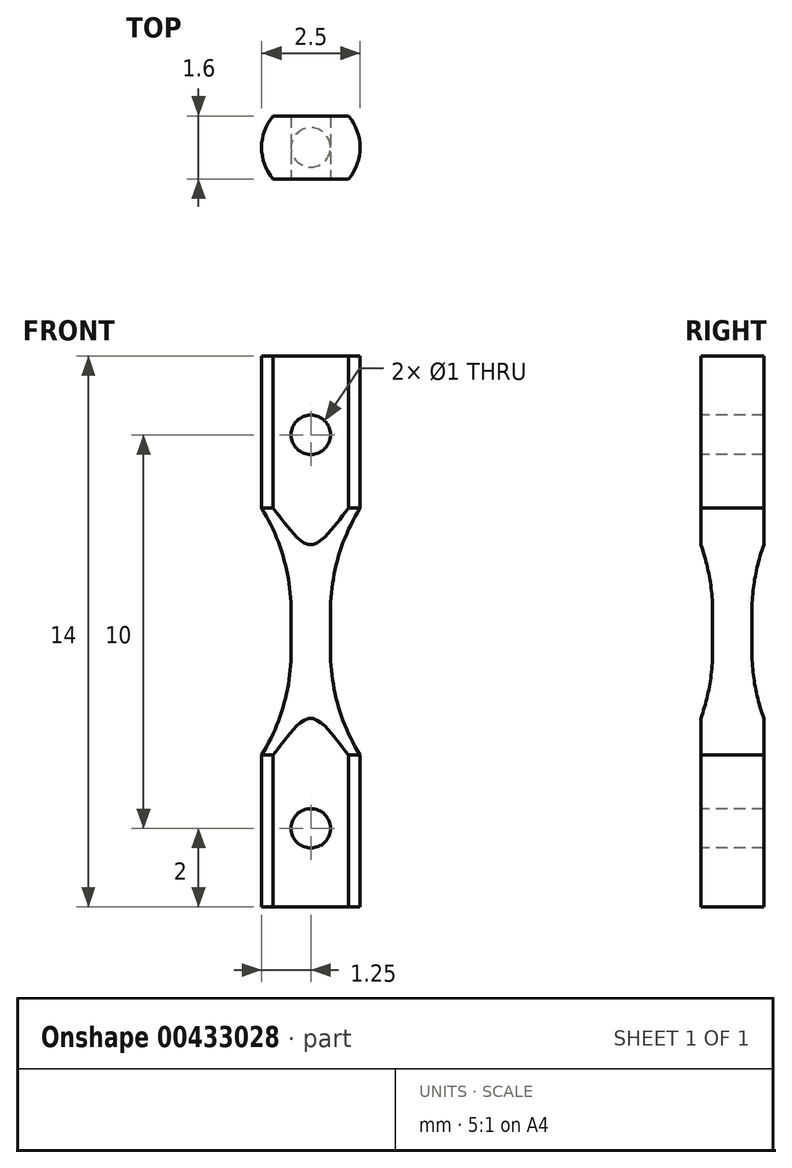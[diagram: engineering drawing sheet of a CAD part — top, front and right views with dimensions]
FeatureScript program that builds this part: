
annotation { "Feature Type Name" : "Feature", "Feature Type Description" : "" }
export const myFeature = defineFeature(function(context is Context, id is Id, definition is map)
    precondition{}
    {
        {
            var Q0;
            Q0=qCreatedBy(makeId("Front.planeOp"),FACE);
            var sketch = newSketch(context, id + "F0", { "sketchPlane" : qUnion([Q0])});
            skLineSegment(sketch, "E0", {"start": v(0, 7) * mm, "end": v(0, 0) * mm});
            skPoint(sketch, "E1", {"position": v(5.5, 0.5) * mm});
            skArc(sketch, "E2", {"start": v(0.5, 0.5) * mm, "mid": v(1.96, 4.04) * mm, "end": v(5.5, 5.5) * mm, "construction": true});
            skLineSegment(sketch, "E3", {"start": v(0, 7) * mm, "end": v(1.25, 7) * mm});
            skLineSegment(sketch, "E4", {"start": v(1.25, 7) * mm, "end": v(1.25, 3.13) * mm});
            skArc(sketch, "E5", {"start": v(0.5, 0.5) * mm, "mid": v(0.7, 1.87) * mm, "end": v(1.25, 3.13) * mm});
            skLineSegment(sketch, "E6.MirrorCS", {"start": v(0, -7) * mm, "end": v(0, 0) * mm});
            skArc(sketch, "E7.MirrorCS", {"start": v(0.5, -0.5) * mm, "mid": v(1.96, -4.04) * mm, "end": v(5.5, -5.5) * mm, "construction": true});
            skLineSegment(sketch, "E8.MirrorCS", {"start": v(1.25, -7) * mm, "end": v(1.25, -3.13) * mm});
            skLineSegment(sketch, "E9.MirrorCS", {"start": v(0, -7) * mm, "end": v(1.25, -7) * mm});
            skArc(sketch, "E10", {"start": v(0.5, -0.5) * mm, "mid": v(0.7, -1.87) * mm, "end": v(1.25, -3.13) * mm});
            skLineSegment(sketch, "E11", {"start": v(0.5, 0.5) * mm, "end": v(0.5, 0.5) * mm});
            skLineSegment(sketch, "E12", {"start": v(0.5, -0.5) * mm, "end": v(0.5, -0.5) * mm});
            skLineSegment(sketch, "E13", {"start": v(0.5, 0.5) * mm, "end": v(0.5, -0.5) * mm});
            skSolve(sketch);
        }
        {
            var Q0;
            {var subQ2=sQuery(id+"F0.wireOp",EDGE,"EKo1FYz1-TvUf-vg46-3QCV-TdD0xKtM2FVf");Q0=makeQuery(id+"F0.imprint","IMPRINT",FACE,{"disambiguationData":[TD([[makeQuery(id+"F0.imprint","IMPRINT",EDGE,{"derivedFrom":subQ2}),1.0]])]});}
            var Q1;
            {var subQ0=sQuery(id+"F0.wireOp",EDGE,"EKo1FYz1-TvUf-vg46-3QCV-TdD0xKtM2FVf");Q1=makeQuery(id+"F0.imprint","IMPRINT",FACE,{"disambiguationData":[TD([[makeQuery(id+"F0.imprint","IMPRINT",EDGE,{"derivedFrom":subQ0}),-1.0]])]});}
            var Q2;
            {var subQ1=sQuery(id+"F0.wireOp",EDGE,"E3");Q2=makeQuery(id+"F0.imprint","IMPRINT",FACE,{"disambiguationData":[TD([[makeQuery(id+"F0.imprint","IMPRINT",EDGE,{"derivedFrom":subQ1}),-1.0]])]});}
            var Q3;
            Q3=sQuery(id+"F0.wireOp",EDGE,"E0");
            revolve(context, id + "F1", {"entities" : qUnion([Q0, Q1, Q2]), "axis" : qUnion([Q3]), "revolveType" : RevolveType.FULL});
        }
        {
            var Q0;
            Q0=qCreatedBy(makeId("Front.planeOp"),FACE);
            var sketch = newSketch(context, id + "F2", { "sketchPlane" : qUnion([Q0])});
            skLineSegment(sketch, "E14", {"start": v(1.25, 7) * mm, "end": v(0, 7) * mm});
            skLineSegment(sketch, "E15", {"start": v(0, 7) * mm, "end": v(0, 0) * mm});
            skLineSegment(sketch, "E16", {"start": v(1.25, 7) * mm, "end": v(1.25, 0) * mm});
            skLineSegment(sketch, "E17", {"start": v(1.25, 0) * mm, "end": v(0, 0) * mm});
            skLineSegment(sketch, "E18.MirrorCS", {"start": v(-1.25, 7) * mm, "end": v(0, 7) * mm});
            skLineSegment(sketch, "E19.MirrorCS", {"start": v(-1.25, 7) * mm, "end": v(-1.25, 0) * mm});
            skLineSegment(sketch, "E20.MirrorCS", {"start": v(-1.25, 0) * mm, "end": v(0, 0) * mm});
            skSolve(sketch);
        }
        {
            var Q0;
            Q0=makeQuery(id+"F2.imprint","IMPRINT",FACE,{"disambiguationData":[TD([[makeQuery(id+"F2.imprint","IMPRINT",EDGE,{"derivedFrom":sQuery(id+"F2.wireOp",EDGE,"E14")}),1.0]])]});
            var Q1;
            Q1=makeQuery(id+"F2.imprint","IMPRINT",FACE,{"disambiguationData":[TD([[makeQuery(id+"F2.imprint","IMPRINT",EDGE,{"derivedFrom":sQuery(id+"F2.wireOp",EDGE,"E15")}),-1.0]])]});
            extrude(context, id + "F3", {"entities" : qUnion([Q0, Q1]), "operationType" : NewBodyOperationType.INTERSECT, "depth" : 1.6 * mm, "symmetric" : true});
        }
        {
            var Q0;
            Q0=qCreatedBy(makeId("Front.planeOp"),FACE);
            var sketch = newSketch(context, id + "F4", { "sketchPlane" : qUnion([Q0])});
            skPoint(sketch, "E21", {"position": v(0, 5) * mm});
            skCircle(sketch, "E22", {"center": v(0, 5) * mm, "radius": 0.5 * mm});
            skSolve(sketch);
        }
        {
            var Q0;
            Q0=makeQuery(id+"F4.imprint","IMPRINT",FACE,{"disambiguationData":[TD([[makeQuery(id+"F4.imprint","IMPRINT",EDGE,{"derivedFrom":sQuery(id+"F4.wireOp",EDGE,"E22")}),1.0]])]});
            extrude(context, id + "F5", {"entities" : qUnion([Q0]), "operationType" : NewBodyOperationType.REMOVE, "oppositeDirection" : true, "depth" : 25 * mm, "symmetric" : true});
        }
        {
            var Q0;
            Q0=makeQuery(id+"F1.opRevolve","SWEPT_BODY",BODY,{"disambiguationData":[OSD([sQuery(id+"F0.wireOp",EDGE,"OcnPvCSy-cZS5-JDQh-wchw-9l9LrSL49Ts8"),sQuery(id+"F0.wireOp",EDGE,"Dct7jnFl-Wa0s-DOEL-NKnk-l80QN2pxv5ud"),sQuery(id+"F0.wireOp",EDGE,"dMe9K8Vx-obDh-k0uA-Upyp-ExFzSnsmPXVj"),sQuery(id+"F0.wireOp",EDGE,"ASEVp0sq-exOI-wicY-23Um-DL8Uq5OcPyFh"),sQuery(id+"F0.wireOp",EDGE,"b3V7QA5D-BfOZ-9Ogp-569r-IGBEo0v84lE0"),sQuery(id+"F0.wireOp",EDGE,"E0"),sQuery(id+"F0.wireOp",EDGE,"FAY0BoeA-ddRC-77QY-SOEF-yvcMaOBgnlRh")])]});
            var Q1;
            Q1=qCreatedBy(makeId("Top.planeOp"),FACE);
            mirror(context, id + "F6", {"operationType" : NewBodyOperationType.ADD, "entities" : qUnion([Q0]), "mirrorPlane" : qUnion([Q1])});
        }
    });
